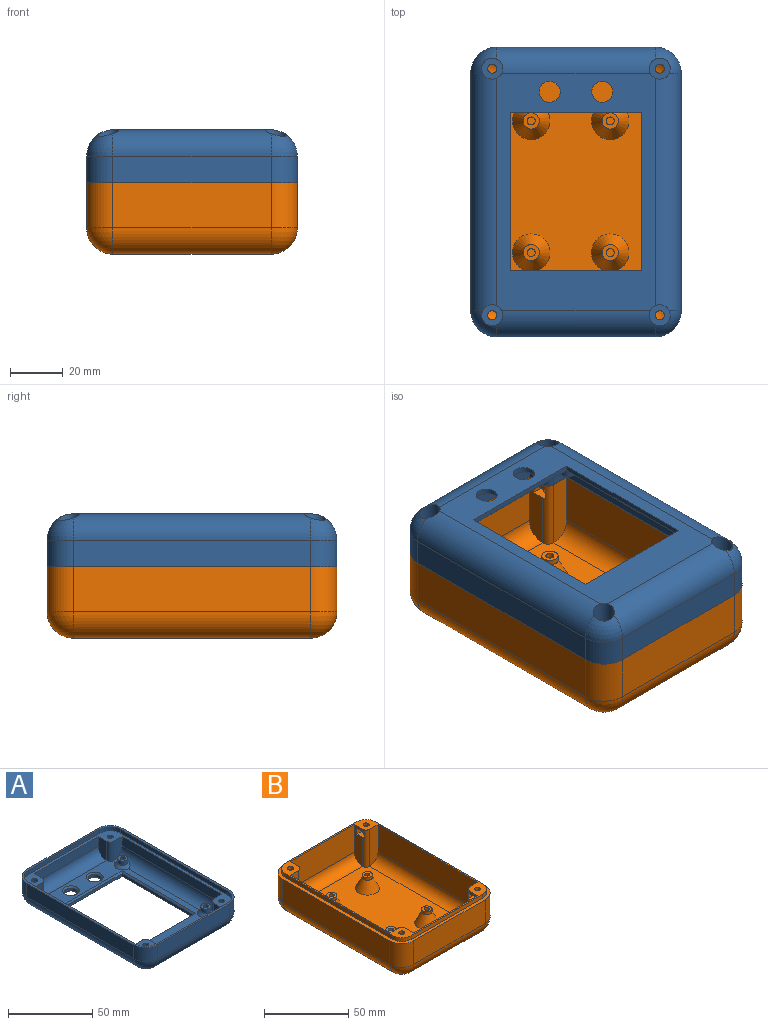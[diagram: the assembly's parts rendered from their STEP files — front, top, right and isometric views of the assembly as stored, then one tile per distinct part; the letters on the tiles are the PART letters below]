
ASSEMBLY  parts=2 mates=1
PART A: 96 faces, bbox 80x110x20 mm
  f0: plane 90x60mm, normal (0,0,1), area 1847.6mm2, adj f1,f2,f19,f21,f37,f38,f39,f40
  f1: cylinder r=7mm len=84mm, axis (0,-1,0), area 851.7mm2, adj f0,f16,f54,f63,f92,f95
  f2: cylinder r=7mm len=84mm, axis (0,1,0), area 851.7mm2, adj f0,f17,f57,f60,f93,f94
  f3: plane 90x60mm, normal (0,0,-1), area 2291.8mm2, adj f4,f6,f7,f9,f31,f32,f33,f34
  f4: cylinder r=10mm len=90mm, axis (0,1,0), area 1394.3mm2, adj f3,f5,f14,f23,f67,f68
  f5: sphere r=10mm, area 123.8mm2, adj f4,f6,f30,f67
  f6: cylinder r=10mm len=60mm, axis (1,0,0), area 923.1mm2, adj f3,f5,f15,f29,f64,f67
  f7: cylinder r=10mm len=60mm, axis (-1,0,0), area 923.1mm2, adj f3,f8,f14,f25,f68,f71
  f8: sphere r=10mm, area 123.8mm2, adj f7,f9,f26,f71
  f9: cylinder r=10mm len=90mm, axis (0,-1,0), area 1394.3mm2, adj f3,f8,f15,f27,f64,f71
  f10: cylinder r=1.75mm len=3.5mm, axis (0,0,1), area 22mm2, adj f51,f70
  f11: cylinder r=1.75mm len=3.5mm, axis (0,0,1), area 22mm2, adj f51,f69
  f12: cylinder r=1.75mm len=3.5mm, axis (0,0,1), area 22mm2, adj f51,f66
  f13: cylinder r=1.75mm len=3.5mm, axis (0,0,1), area 22mm2, adj f51,f65
  f14: sphere r=10mm, area 123.8mm2, adj f4,f7,f24,f68
  f15: sphere r=10mm, area 123.8mm2, adj f6,f9,f28,f64
  f16: plane 84x7mm, normal (1,0,0), area 588mm2, adj f1,f51,f54,f63
  f17: plane 84x7mm, normal (-1,0,0), area 588mm2, adj f2,f51,f57,f60
  f18: plane 54x7mm, normal (0,1,0), area 378mm2, adj f19,f51,f58,f62
  f19: cylinder r=7mm len=54mm, axis (1,0,0), area 593.8mm2, adj f0,f18,f58,f62
  f20: plane 54x7mm, normal (0,-1,0), area 378mm2, adj f21,f51,f52,f56
  f21: cylinder r=7mm len=54mm, axis (-1,0,0), area 593.8mm2, adj f0,f20,f52,f56
  f22: plane 110x80mm, normal (0,0,1), area 484.1mm2, adj f23,f24,f25,f26,f27,f28,f29,f30
  f23: plane 90x10mm, normal (1,0,0), area 900mm2, adj f4,f22,f24,f30
  f24: cylinder r=10mm len=10mm, axis (0,0,-1), area 157.1mm2, adj f14,f22,f23,f25
  f25: plane 60x10mm, normal (0,1,0), area 600mm2, adj f7,f22,f24,f26
  f26: cylinder r=10mm len=10mm, axis (0,0,-1), area 157.1mm2, adj f8,f22,f25,f27
  f27: plane 90x10mm, normal (-1,0,0), area 900mm2, adj f9,f22,f26,f28
  f28: cylinder r=10mm len=10mm, axis (0,0,-1), area 157.1mm2, adj f15,f22,f27,f29
  f29: plane 60x10mm, normal (0,-1,0), area 600mm2, adj f6,f22,f28,f30
  f30: cylinder r=10mm len=10mm, axis (0,0,-1), area 157.1mm2, adj f5,f22,f23,f29
  f31: cylinder r=4mm len=8mm, axis (0,0,1), area 50.3mm2, adj f3,f37
  f32: cylinder r=4mm len=8mm, axis (0,0,1), area 50.3mm2, adj f3,f38
  f33: plane 60x2mm, normal (1,0,0), area 120mm2, adj f3,f34,f35,f39
  f34: plane 50x2mm, normal (0,-1,0), area 100mm2, adj f3,f33,f36,f40
  f35: plane 50x2mm, normal (0,1,0), area 100mm2, adj f3,f33,f36,f41
  f36: plane 60x2mm, normal (-1,0,0), area 120mm2, adj f3,f34,f35,f42
  f37: cone r=4mm half-angle=45deg, axis (0,0,1), area 40mm2, adj f0,f31
  f38: cone r=4mm half-angle=45deg, axis (0,0,1), area 40mm2, adj f0,f32
  f39: plane 62x1mm, normal (0.71,0,0.71), area 86.3mm2, adj f0,f33,f40,f41
  f40: plane 52x1mm, normal (0,-0.71,0.71), area 72.1mm2, adj f0,f34,f39,f42
  f41: plane 52x1mm, normal (0,0.71,0.71), area 72.1mm2, adj f0,f35,f39,f42
  f42: plane 62x1mm, normal (-0.71,0,0.71), area 86.3mm2, adj f0,f36,f40,f41
  f43: plane 90x3mm, normal (1,0,0), area 270mm2, adj f22,f44,f50,f51
  f44: cylinder r=8.65mm len=8.65mm, axis (0,0,1), area 40.8mm2, adj f22,f43,f45,f51
  f45: plane 60x3mm, normal (0,1,0), area 180mm2, adj f22,f44,f46,f51
  f46: cylinder r=8.65mm len=8.65mm, axis (0,0,1), area 40.8mm2, adj f22,f45,f47,f51
  f47: plane 90x3mm, normal (-1,0,0), area 270mm2, adj f22,f46,f48,f51
  f48: cylinder r=8.65mm len=8.65mm, axis (0,0,1), area 40.8mm2, adj f22,f47,f49,f51
  f49: plane 60x3mm, normal (0,-1,0), area 180mm2, adj f22,f48,f50,f51
  f50: cylinder r=8.65mm len=8.65mm, axis (0,0,1), area 40.8mm2, adj f22,f43,f49,f51
  f51: plane 107.3x77.3mm, normal (0,0,1), area 887.9mm2, adj f10,f11,f12,f13,f16,f17,f18,f20
  f52: plane 14x7mm, normal (1,0,0), area 87.5mm2, adj f20,f21,f51,f53
  f53: cylinder r=3mm len=14mm, axis (0,0,1), area 66mm2, adj f0,f51,f52,f54
  f54: plane 14x7mm, normal (0,-1,0), area 87.5mm2, adj f1,f16,f51,f53
  f55: cylinder r=3mm len=14mm, axis (0,0,1), area 66mm2, adj f0,f51,f56,f57
  f56: plane 14x7mm, normal (-1,0,0), area 87.5mm2, adj f20,f21,f51,f55
  f57: plane 14x7mm, normal (0,-1,0), area 87.5mm2, adj f2,f17,f51,f55
  f58: plane 14x7mm, normal (-1,0,0), area 87.5mm2, adj f18,f19,f51,f59
  f59: cylinder r=3mm len=14mm, axis (0,0,1), area 66mm2, adj f0,f51,f58,f60
  f60: plane 14x7mm, normal (0,1,0), area 87.5mm2, adj f2,f17,f51,f59
  f61: cylinder r=3mm len=14mm, axis (0,0,1), area 66mm2, adj f0,f51,f62,f63
  f62: plane 14x7mm, normal (1,0,0), area 87.5mm2, adj f18,f19,f51,f61
  f63: plane 14x7mm, normal (0,1,0), area 87.5mm2, adj f1,f16,f51,f61
  f64: cylinder r=4mm len=15mm, axis (0,0,-1), area 348.3mm2, adj f3,f6,f9,f15,f65
  f65: plane 8x8mm, normal (0,0,-1), area 40.6mm2, adj f13,f64
  f66: plane 8x8mm, normal (0,0,-1), area 40.6mm2, adj f12,f67
  f67: cylinder r=4mm len=15mm, axis (0,0,-1), area 348.2mm2, adj f3,f4,f5,f6,f66
  f68: cylinder r=4mm len=15mm, axis (0,0,-1), area 348.2mm2, adj f3,f4,f7,f14,f69
  f69: plane 8x8mm, normal (0,0,-1), area 40.6mm2, adj f11,f68
  f70: plane 8x8mm, normal (0,0,-1), area 40.6mm2, adj f10,f71
  f71: cylinder r=4mm len=15mm, axis (0,0,-1), area 348.3mm2, adj f3,f7,f8,f9,f70
  f72: plane 6.2x6.2mm, normal (0,0,1), area 23.1mm2, adj f73,f74
  f73: cylinder r=3.1mm len=6.2mm, axis (0,0,1), area 58.4mm2, adj f72,f95
  f74: cylinder r=1.5mm len=5mm, axis (0,0,1), area 46.3mm2, adj f72,f75,f76
  f75: cylinder r=7mm len=3mm, axis (0,-1,0), area 5.1mm2, adj f74,f76
  f76: plane 2.83x1mm, normal (0,0,1), area 2.1mm2, adj f74,f75
  f77: cylinder r=3.1mm len=6.2mm, axis (0,0,1), area 58.4mm2, adj f79,f94
  f78: cylinder r=1.5mm len=5mm, axis (0,0,1), area 46.3mm2, adj f79,f80,f81
  f79: plane 6.2x6.2mm, normal (0,0,1), area 23.1mm2, adj f77,f78
  f80: cylinder r=7mm len=3mm, axis (0,1,0), area 5.1mm2, adj f78,f81
  f81: plane 2.83x1mm, normal (0,0,1), area 2.1mm2, adj f78,f80
  f82: plane 6.2x6.2mm, normal (0,0,1), area 23.1mm2, adj f83,f84
  f83: cylinder r=1.5mm len=5mm, axis (0,0,1), area 46.3mm2, adj f82,f85,f86
  f84: cylinder r=3.1mm len=6.2mm, axis (0,0,1), area 58.4mm2, adj f82,f92
  f85: cylinder r=7mm len=3mm, axis (0,-1,0), area 5.1mm2, adj f83,f86
  f86: plane 2.83x1mm, normal (0,0,1), area 2.1mm2, adj f83,f85
  f87: cylinder r=1.5mm len=5mm, axis (0,0,1), area 46.3mm2, adj f89,f90,f91
  f88: cylinder r=3.1mm len=6.2mm, axis (0,0,1), area 58.4mm2, adj f89,f93
  f89: plane 6.2x6.2mm, normal (0,0,1), area 23.1mm2, adj f87,f88
  f90: cylinder r=7mm len=3mm, axis (0,1,0), area 5.1mm2, adj f87,f91
  f91: plane 2.83x1mm, normal (0,0,1), area 2.1mm2, adj f87,f90
  f92: cone r=3.1mm half-angle=45deg, axis (0,0,-1), area 56.1mm2, adj f0,f1,f84
  f93: cone r=5.1mm half-angle=45deg, axis (0,0,-1), area 56.1mm2, adj f0,f2,f88
  f94: cone r=3.1mm half-angle=45deg, axis (0,0,-1), area 56.1mm2, adj f0,f2,f77
  f95: cone r=5.1mm half-angle=45deg, axis (0,0,-1), area 56.1mm2, adj f0,f1,f73
PART B: 104 faces, bbox 80x110x30 mm
  f0: cylinder r=3mm len=27mm, axis (0,0,1), area 122.3mm2, adj f1,f10,f17,f45,f76,f77,f80
  f1: plane 27x7mm, normal (1,0,0), area 159.3mm2, adj f0,f14,f16,f17,f76,f77,f81
  f2: plane 27x7mm, normal (-1,0,0), area 159.3mm2, adj f3,f14,f16,f17,f68,f70,f71
  f3: cylinder r=3mm len=27mm, axis (0,0,1), area 122.3mm2, adj f2,f10,f17,f46,f68,f71,f73
  f4: cylinder r=3mm len=27mm, axis (0,0,1), area 122.3mm2, adj f5,f10,f17,f48,f60,f63,f65
  f5: plane 27x7mm, normal (1,0,0), area 159.3mm2, adj f4,f9,f12,f17,f60,f62,f63
  f6: plane 27x7mm, normal (-1,0,0), area 159.3mm2, adj f7,f9,f12,f17,f52,f53,f57
  f7: cylinder r=3mm len=27mm, axis (0,0,1), area 122.3mm2, adj f6,f10,f17,f51,f52,f53,f55
  f8: plane 84x20mm, normal (-1,0,0), area 1680mm2, adj f15,f17,f46,f51
  f9: plane 54x20mm, normal (0,1,0), area 1080mm2, adj f5,f6,f12,f17
  f10: plane 90x60mm, normal (0,0,1), area 4738.3mm2, adj f0,f3,f4,f7,f12,f13,f15,f16
  f11: plane 84x20mm, normal (1,0,0), area 1680mm2, adj f13,f17,f45,f48
  f12: cylinder r=7mm len=54mm, axis (1,0,0), area 593.8mm2, adj f5,f6,f9,f10
  f13: cylinder r=7mm len=84mm, axis (0,-1,0), area 923.6mm2, adj f10,f11,f45,f48
  f14: plane 54x20mm, normal (0,-1,0), area 1080mm2, adj f1,f2,f16,f17
  f15: cylinder r=7mm len=84mm, axis (0,1,0), area 923.6mm2, adj f8,f10,f46,f51
  f16: cylinder r=7mm len=54mm, axis (-1,0,0), area 593.8mm2, adj f1,f2,f10,f14
  f17: plane 105.6x75.6mm, normal (0,0,1), area 588.9mm2, adj f0,f1,f2,f3,f4,f5,f6,f7
  f18: cylinder r=7.8mm len=7.8mm, axis (0,0,1), area 34.3mm2, adj f17,f19,f25,f26
  f19: plane 90x2.8mm, normal (-1,0,0), area 252mm2, adj f17,f18,f20,f26
  f20: cylinder r=7.8mm len=7.8mm, axis (0,0,1), area 34.3mm2, adj f17,f19,f21,f26
  f21: plane 60x2.8mm, normal (0,1,0), area 168mm2, adj f17,f20,f22,f26
  f22: cylinder r=7.8mm len=7.8mm, axis (0,0,1), area 34.3mm2, adj f17,f21,f23,f26
  f23: plane 90x2.8mm, normal (1,0,0), area 252mm2, adj f17,f22,f24,f26
  f24: cylinder r=7.8mm len=7.8mm, axis (0,0,1), area 34.3mm2, adj f17,f23,f25,f26
  f25: plane 60x2.8mm, normal (0,-1,0), area 168mm2, adj f17,f18,f24,f26
  f26: plane 110x80mm, normal (0,0,1), area 783mm2, adj f18,f19,f20,f21,f22,f23,f24,f25
  f27: plane 90x60mm, normal (0,0,-1), area 5400mm2, adj f28,f30,f32,f34
  f28: cylinder r=10mm len=90mm, axis (0,1,0), area 1413.7mm2, adj f27,f29,f35,f43
  f29: sphere r=10mm, area 157.1mm2, adj f28,f30,f42
  f30: cylinder r=10mm len=60mm, axis (-1,0,0), area 942.5mm2, adj f27,f29,f31,f41
  f31: sphere r=10mm, area 157.1mm2, adj f30,f32,f40
  f32: cylinder r=10mm len=90mm, axis (0,-1,0), area 1413.7mm2, adj f27,f31,f33,f39
  f33: sphere r=10mm, area 157.1mm2, adj f32,f34,f38
  f34: cylinder r=10mm len=60mm, axis (1,0,0), area 942.5mm2, adj f27,f33,f35,f37
  f35: sphere r=10mm, area 157.1mm2, adj f28,f34,f36
  f36: cylinder r=10mm len=17.2mm, axis (0,0,-1), area 270.2mm2, adj f26,f35,f37,f43
  f37: plane 60x17.2mm, normal (0,-1,0), area 1032mm2, adj f26,f34,f36,f38
  f38: cylinder r=10mm len=17.2mm, axis (0,0,-1), area 270.2mm2, adj f26,f33,f37,f39
  f39: plane 90x17.2mm, normal (-1,0,0), area 1548mm2, adj f26,f32,f38,f40
  f40: cylinder r=10mm len=17.2mm, axis (0,0,-1), area 270.2mm2, adj f26,f31,f39,f41
  f41: plane 60x17.2mm, normal (0,1,0), area 1032mm2, adj f26,f30,f40,f42
  f42: cylinder r=10mm len=17.2mm, axis (0,0,-1), area 270.2mm2, adj f26,f29,f41,f43
  f43: plane 90x17.2mm, normal (1,0,0), area 1548mm2, adj f26,f28,f36,f42
  f44: cylinder r=1.75mm len=3.5mm, axis (0,0,1), area 22mm2, adj f17,f77
  f45: plane 27x7mm, normal (0,-1,0), area 178.5mm2, adj f0,f11,f13,f17
  f46: plane 27x7mm, normal (0,-1,0), area 178.5mm2, adj f3,f8,f15,f17
  f47: cylinder r=1.75mm len=3.5mm, axis (0,0,1), area 22mm2, adj f17,f71
  f48: plane 27x7mm, normal (0,1,0), area 178.5mm2, adj f4,f11,f13,f17
  f49: cylinder r=1.75mm len=3.5mm, axis (0,0,1), area 22mm2, adj f17,f63
  f50: cylinder r=1.75mm len=3.5mm, axis (0,0,1), area 22mm2, adj f17,f53
  f51: plane 27x7mm, normal (0,1,0), area 178.5mm2, adj f7,f8,f15,f17
  f52: plane 8.26x6mm, normal (0,0,1), area 34.7mm2, adj f6,f7,f54,f55,f56,f57,f59
  f53: plane 8.26x6mm, normal (0,0,-1), area 34.7mm2, adj f6,f7,f50,f54,f55,f56,f57
  f54: plane 4x3mm, normal (-0.87,-0.5,0), area 13.9mm2, adj f52,f53,f55,f56
  f55: plane 6.28x4mm, normal (0,-1,0), area 25.1mm2, adj f7,f52,f53,f54
  f56: plane 4x3mm, normal (-0.87,0.5,0), area 13.9mm2, adj f52,f53,f54,f57
  f57: plane 6.53x4mm, normal (0,1,0), area 26.1mm2, adj f6,f52,f53,f56
  f58: sphere r=7mm, area 10.6mm2, adj f59
  f59: cylinder r=1.75mm len=20.95mm, axis (0,0,1), area 222.8mm2, adj f52,f58
  f60: plane 8.26x6mm, normal (0,0,1), area 34.7mm2, adj f4,f5,f61,f62,f64,f65,f67
  f61: plane 4x3mm, normal (0.87,0.5,0), area 13.9mm2, adj f60,f62,f63,f64
  f62: plane 6.53x4mm, normal (0,1,0), area 26.1mm2, adj f5,f60,f61,f63
  f63: plane 8.26x6mm, normal (0,0,-1), area 34.7mm2, adj f4,f5,f49,f61,f62,f64,f65
  f64: plane 4x3mm, normal (0.87,-0.5,0), area 13.9mm2, adj f60,f61,f63,f65
  f65: plane 6.28x4mm, normal (0,-1,0), area 25.1mm2, adj f4,f60,f63,f64
  f66: sphere r=7mm, area 10.6mm2, adj f67
  f67: cylinder r=1.75mm len=20.95mm, axis (0,0,1), area 223.2mm2, adj f60,f66
  f68: plane 8.26x6mm, normal (0,0,1), area 34.7mm2, adj f2,f3,f69,f70,f72,f73,f75
  f69: plane 4x3mm, normal (-0.87,-0.5,0), area 13.9mm2, adj f68,f70,f71,f72
  f70: plane 6.53x4mm, normal (0,-1,0), area 26.1mm2, adj f2,f68,f69,f71
  f71: plane 8.26x6mm, normal (0,0,-1), area 34.7mm2, adj f2,f3,f47,f69,f70,f72,f73
  f72: plane 4x3mm, normal (-0.87,0.5,0), area 13.9mm2, adj f68,f69,f71,f73
  f73: plane 6.28x4mm, normal (0,1,0), area 25.1mm2, adj f3,f68,f71,f72
  f74: sphere r=7mm, area 10.6mm2, adj f75
  f75: cylinder r=1.75mm len=20.95mm, axis (0,0,1), area 222.3mm2, adj f68,f74
  f76: plane 8.26x6mm, normal (0,0,1), area 34.7mm2, adj f0,f1,f78,f79,f80,f81,f83
  f77: plane 8.26x6mm, normal (0,0,-1), area 34.7mm2, adj f0,f1,f44,f78,f79,f80,f81
  f78: plane 4x3mm, normal (0.87,-0.5,0), area 13.9mm2, adj f76,f77,f79,f81
  f79: plane 4x3mm, normal (0.87,0.5,0), area 13.9mm2, adj f76,f77,f78,f80
  f80: plane 6.28x4mm, normal (0,1,0), area 25.1mm2, adj f0,f76,f77,f79
  f81: plane 6.53x4mm, normal (0,-1,0), area 26.1mm2, adj f1,f76,f77,f78
  f82: sphere r=7mm, area 10.6mm2, adj f83
  f83: cylinder r=1.75mm len=20.95mm, axis (0,0,1), area 222.8mm2, adj f76,f82
  f84: cylinder r=1.5mm len=10mm, axis (0,0,1), area 94.2mm2, adj f86,f87
  f85: cylinder r=3.1mm len=6.2mm, axis (0,0,1), area 39mm2, adj f86,f103
  f86: plane 6.2x6.2mm, normal (0,0,1), area 23.1mm2, adj f84,f85
  f87: plane 3x3mm, normal (0,0,1), area 7.1mm2, adj f84
  f88: cylinder r=1.5mm len=10mm, axis (0,0,1), area 94.2mm2, adj f90,f91
  f89: cylinder r=3.1mm len=6.2mm, axis (0,0,1), area 39mm2, adj f90,f102
  f90: plane 6.2x6.2mm, normal (0,0,1), area 23.1mm2, adj f88,f89
  f91: plane 3x3mm, normal (0,0,1), area 7.1mm2, adj f88
  f92: cylinder r=1.5mm len=10mm, axis (0,0,1), area 94.2mm2, adj f94,f95
  f93: cylinder r=3.1mm len=6.2mm, axis (0,0,1), area 39mm2, adj f94,f101
  f94: plane 6.2x6.2mm, normal (0,0,1), area 23.1mm2, adj f92,f93
  f95: plane 3x3mm, normal (0,0,1), area 7.1mm2, adj f92
  f96: cylinder r=1.5mm len=10mm, axis (0,0,1), area 94.2mm2, adj f98,f99
  f97: cylinder r=3.1mm len=6.2mm, axis (0,0,1), area 39mm2, adj f98,f100
  f98: plane 6.2x6.2mm, normal (0,0,1), area 23.1mm2, adj f96,f97
  f99: plane 3x3mm, normal (0,0,1), area 7.1mm2, adj f96
  f100: cone r=3.1mm half-angle=26.6deg, axis (0,0,-1), area 286.6mm2, adj f10,f97
  f101: cone r=3.1mm half-angle=26.6deg, axis (0,0,-1), area 286.6mm2, adj f10,f93
  f102: cone r=3.1mm half-angle=26.6deg, axis (0,0,-1), area 286.6mm2, adj f10,f89
  f103: cone r=3.1mm half-angle=26.6deg, axis (0,0,-1), area 286.6mm2, adj f10,f85
PLACE A rot(axis=(0,1,0),180deg) t=(50.3,-18.33,68.68)mm
PLACE B t=(50.3,-18.33,21.48)mm
MATE fastened B.f3 <-> A.f26  axis (0,0,1) through (80.3,26.67,48.68)mm
